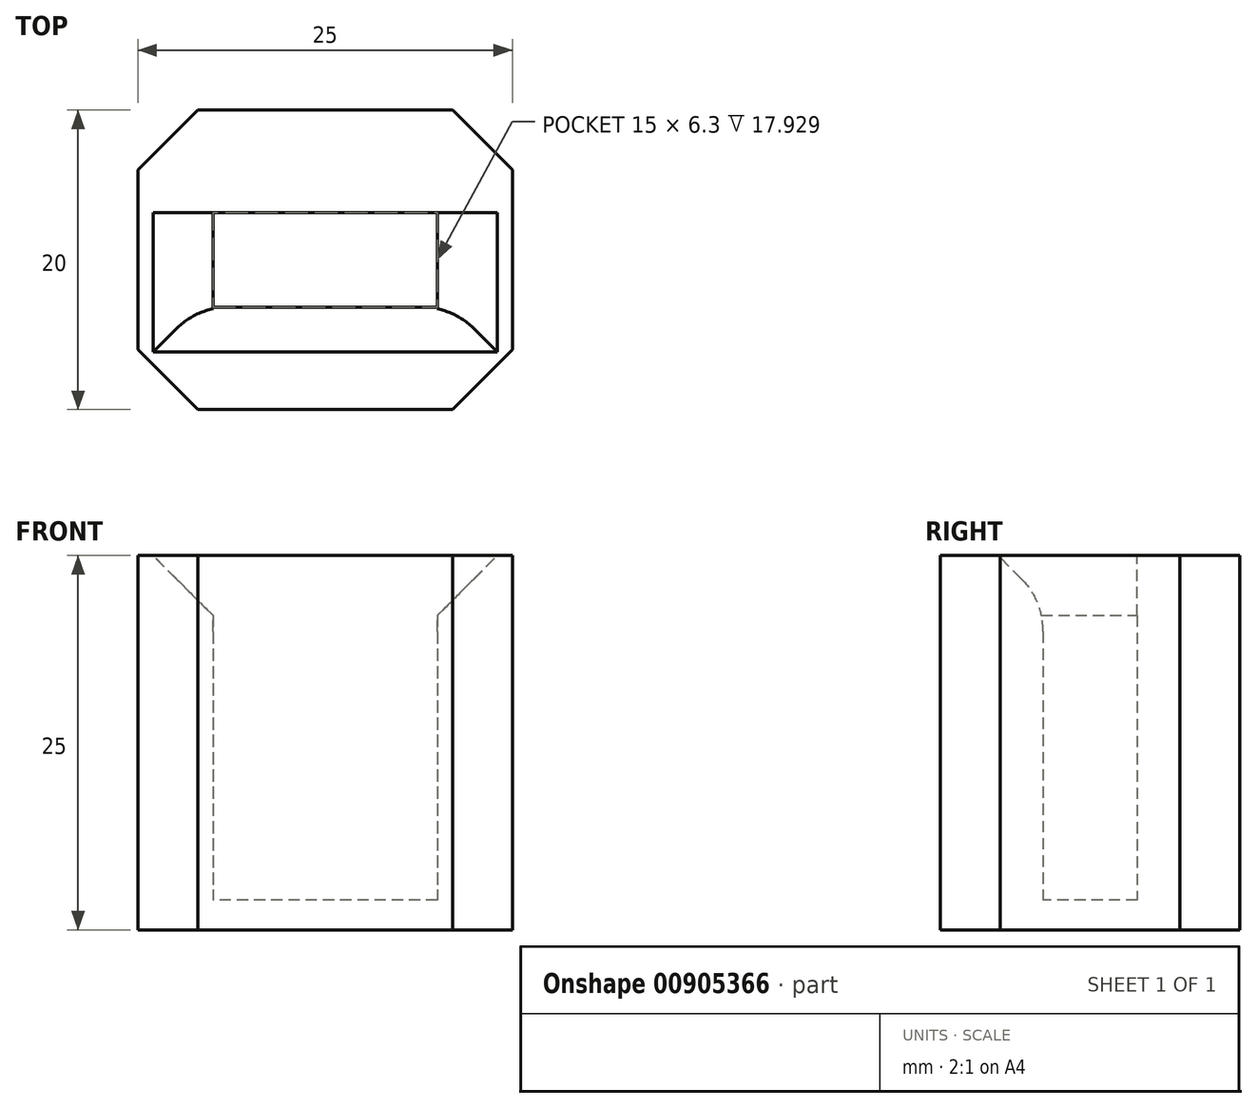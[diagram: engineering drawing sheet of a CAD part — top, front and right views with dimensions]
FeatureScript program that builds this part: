
annotation { "Feature Type Name" : "Feature", "Feature Type Description" : "" }
export const myFeature = defineFeature(function(context is Context, id is Id, definition is map)
    precondition{}
    {
        {
            var Q0;
            Q0=qCreatedBy(makeId("Top.planeOp"),FACE);
            var sketch = newSketch(context, id + "F0", { "sketchPlane" : qUnion([Q0])});
            skLineSegment(sketch, "E0.bottom", {"start": v(12.5, 10) * mm, "end": v(-12.5, 10) * mm});
            skLineSegment(sketch, "E0.top", {"start": v(12.5, -10) * mm, "end": v(-12.5, -10) * mm});
            skLineSegment(sketch, "E0.left", {"start": v(12.5, 10) * mm, "end": v(12.5, -10) * mm});
            skLineSegment(sketch, "E0.right", {"start": v(-12.5, 10) * mm, "end": v(-12.5, -10) * mm});
            skPoint(sketch, "E0.middle", {"position": v(0, 0) * mm});
            skLineSegment(sketch, "E1.bottom", {"start": v(7.5, 3.15) * mm, "end": v(-7.5, 3.15) * mm});
            skLineSegment(sketch, "E1.top", {"start": v(7.5, -3.15) * mm, "end": v(-7.5, -3.15) * mm});
            skLineSegment(sketch, "E1.left", {"start": v(7.5, 3.15) * mm, "end": v(7.5, -3.15) * mm});
            skLineSegment(sketch, "E1.right", {"start": v(-7.5, 3.15) * mm, "end": v(-7.5, -3.15) * mm});
            skSolve(sketch);
        }
        {
            var Q0;
            Q0 = qSketchRegion(id + "F0", true);
            extrude(context, id + "F1", {"entities" : qUnion([Q0]), "depth" : 25 * mm, "offsetDistance" : 25 * mm});
        }
        {
            var Q0;
            Q0=makeQuery(id+"F1.opExtrude","CAP_FACE",FACE,{"disambiguationData":[OSD([sQuery(id+"F0.wireOp",EDGE,"E0.bottom"),sQuery(id+"F0.wireOp",EDGE,"E0.top"),sQuery(id+"F0.wireOp",EDGE,"E0.left"),sQuery(id+"F0.wireOp",EDGE,"E0.right"),sQuery(id+"F0.wireOp",EDGE,"E1.bottom"),sQuery(id+"F0.wireOp",EDGE,"E1.top"),sQuery(id+"F0.wireOp",EDGE,"E1.left"),sQuery(id+"F0.wireOp",EDGE,"E1.right")])],"isStart":true});
            var sketch = newSketch(context, id + "F2", { "sketchPlane" : qUnion([Q0])});
            skLineSegment(sketch, "E2.bottom", {"start": v(12.5, 10) * mm, "end": v(-12.5, 10) * mm});
            skLineSegment(sketch, "E2.top", {"start": v(12.5, -10) * mm, "end": v(-12.5, -10) * mm});
            skLineSegment(sketch, "E2.left", {"start": v(12.5, 10) * mm, "end": v(12.5, -10) * mm});
            skLineSegment(sketch, "E2.right", {"start": v(-12.5, 10) * mm, "end": v(-12.5, -10) * mm});
            skPoint(sketch, "E2.middle", {"position": v(0, 0) * mm});
            skSolve(sketch);
        }
        {
            var Q0;
            Q0=makeQuery(id+"F2.imprint","IMPRINT",FACE,{"disambiguationData":[TD([[makeQuery(id+"F2.imprint","IMPRINT",EDGE,{"derivedFrom":makeQuery(id+"F1.opExtrude","CAP_EDGE",EDGE,{"disambiguationData":[OSD([sQuery(id+"F0.wireOp",EDGE,"E1.bottom")])],"isStart":true})}),-1.0]])]});
            extrude(context, id + "F3", {"entities" : qUnion([Q0]), "operationType" : NewBodyOperationType.ADD, "oppositeDirection" : true, "depth" : 2 * mm, "offsetDistance" : 25 * mm});
        }
        {
            var Q0;
            Q0=makeQuery(id+"F1.opExtrude","CAP_EDGE",EDGE,{"disambiguationData":[OSD([sQuery(id+"F0.wireOp",EDGE,"E1.right")])],"isStart":false});
            var Q1;
            Q1=makeQuery(id+"F1.opExtrude","CAP_EDGE",EDGE,{"disambiguationData":[OSD([sQuery(id+"F0.wireOp",EDGE,"E1.left")])],"isStart":false});
            var Q2;
            Q2=makeQuery(id+"F1.opExtrude","SWEPT_EDGE",EDGE,{"disambiguationData":[OSD([sQuery(id+"F0.wireOp",EDGE,"E0.top"),sQuery(id+"F0.wireOp",EDGE,"E0.right")])]});
            var Q3;
            Q3=makeQuery(id+"F1.opExtrude","SWEPT_EDGE",EDGE,{"disambiguationData":[OSD([sQuery(id+"F0.wireOp",EDGE,"E0.top"),sQuery(id+"F0.wireOp",EDGE,"E0.left")])]});
            var Q4;
            Q4=makeQuery(id+"F1.opExtrude","SWEPT_EDGE",EDGE,{"disambiguationData":[OSD([sQuery(id+"F0.wireOp",EDGE,"E0.bottom"),sQuery(id+"F0.wireOp",EDGE,"E0.left")])]});
            var Q5;
            Q5=makeQuery(id+"F1.opExtrude","SWEPT_EDGE",EDGE,{"disambiguationData":[OSD([sQuery(id+"F0.wireOp",EDGE,"E0.bottom"),sQuery(id+"F0.wireOp",EDGE,"E0.right")])]});
            chamfer(context, id + "F4", {"entities" : qUnion([Q0, Q1, Q2, Q3, Q4, Q5]), "width" : 4 * mm, "tangentPropagation" : true});
        }
        {
            var Q0;
            Q0=makeQuery(id+"F1.opExtrude","CAP_EDGE",EDGE,{"disambiguationData":[OSD([sQuery(id+"F0.wireOp",EDGE,"E1.top")])],"isStart":false});
            chamfer(context, id + "F5", {"entities" : qUnion([Q0]), "width" : 3 * mm, "tangentPropagation" : true});
        }
        {
            var Q0;
            {var subQ0=sQuery(id+"F0.wireOp",EDGE,"E1.top");Q0=makeQuery(id+"F5.opChamfer","BLEND_EDGE",EDGE,{"blendedFrom":[makeQuery(id+"F1.opExtrude","CAP_EDGE",EDGE,{"disambiguationData":[OSD([subQ0])],"isStart":false}),makeQuery(id+"F1.opExtrude","SWEPT_FACE",FACE,{"disambiguationData":[OSD([subQ0])]})],"blendedInto":[makeQuery(id+"F1.opExtrude","SWEPT_FACE",FACE,{"disambiguationData":[OSD([subQ0])]})]});}
            fillet(context, id + "F6", {"entities" : qUnion([Q0]), "radius" : 5 * mm, "tangentPropagation" : true, "allowEdgeOverflow" : false});
        }
    });
